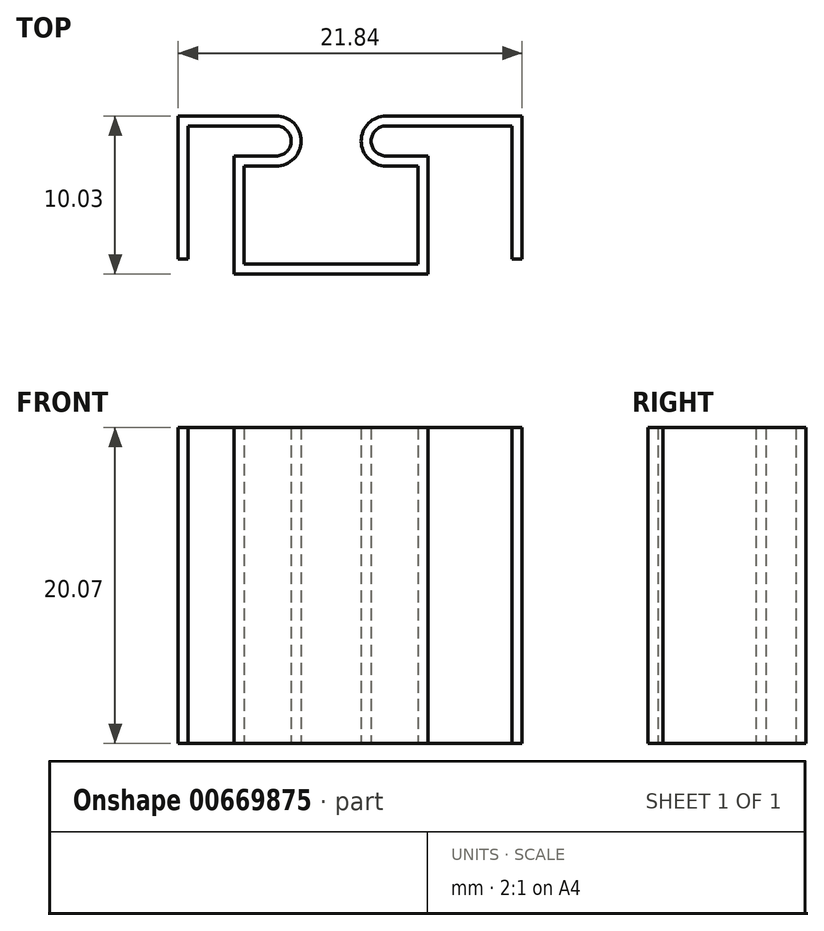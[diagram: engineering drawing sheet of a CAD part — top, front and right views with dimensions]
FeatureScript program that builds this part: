
annotation { "Feature Type Name" : "Feature", "Feature Type Description" : "" }
export const myFeature = defineFeature(function(context is Context, id is Id, definition is map)
    precondition{}
    {
        {
            var Q0;
            Q0=qCreatedBy(makeId("Top.planeOp"),FACE);
            var sketch = newSketch(context, id + "F0", { "sketchPlane" : qUnion([Q0])});
            skLineSegment(sketch, "E0", {"start": v(0, 0) * mm, "end": v(0, 9.1) * mm});
            skLineSegment(sketch, "E1", {"start": v(0, 9.1) * mm, "end": v(6.22, 9.1) * mm});
            skLineSegment(sketch, "E2", {"start": v(4.2, 5.92) * mm, "end": v(4.2, -0.3) * mm});
            skLineSegment(sketch, "E3", {"start": v(4.2, -0.3) * mm, "end": v(15.24, -0.3) * mm});
            skArc(sketch, "E4", {"start": v(6.22, 5.92) * mm, "mid": v(7.81, 7.5) * mm, "end": v(6.22, 9.1) * mm});
            skLineSegment(sketch, "E5", {"start": v(6.22, 5.92) * mm, "end": v(4.2, 5.92) * mm});
            skLineSegment(sketch, "E6.MirrorCS", {"start": v(15.24, 5.92) * mm, "end": v(15.24, -0.3) * mm});
            skLineSegment(sketch, "E7.MirrorCS", {"start": v(13.2, 5.92) * mm, "end": v(15.24, 5.92) * mm});
            skArc(sketch, "E8.MirrorCS", {"start": v(13.2, 5.92) * mm, "mid": v(11.62, 7.5) * mm, "end": v(13.2, 9.1) * mm});
            skLineSegment(sketch, "E9.MirrorCS", {"start": v(21.84, 9.1) * mm, "end": v(13.2, 9.1) * mm});
            skLineSegment(sketch, "E10.MirrorCS", {"start": v(21.84, 0) * mm, "end": v(21.84, 9.1) * mm});
            skLineSegment(sketch, "E11.0", {"start": v(21.2, 0) * mm, "end": v(21.2, 8.46) * mm});
            skArc(sketch, "E11.3", {"start": v(13.2, 6.55) * mm, "mid": v(12.26, 7.5) * mm, "end": v(13.2, 8.46) * mm});
            skArc(sketch, "E11.4", {"start": v(6.22, 6.55) * mm, "mid": v(7.18, 7.5) * mm, "end": v(6.22, 8.46) * mm});
            skLineSegment(sketch, "E11.6", {"start": v(0.63, 8.46) * mm, "end": v(6.22, 8.46) * mm});
            skLineSegment(sketch, "E11.7", {"start": v(0.63, 0) * mm, "end": v(0.63, 8.46) * mm});
            skLineSegment(sketch, "E11.8", {"start": v(6.22, 6.55) * mm, "end": v(3.56, 6.55) * mm});
            skLineSegment(sketch, "E11.9", {"start": v(3.56, 6.55) * mm, "end": v(3.56, -0.94) * mm});
            skLineSegment(sketch, "E11.10", {"start": v(3.56, -0.94) * mm, "end": v(15.88, -0.94) * mm});
            skLineSegment(sketch, "E11.12", {"start": v(15.88, 6.55) * mm, "end": v(15.88, -0.94) * mm});
            skLineSegment(sketch, "E11.13", {"start": v(13.2, 6.55) * mm, "end": v(15.88, 6.55) * mm});
            skLineSegment(sketch, "E12", {"start": v(0.63, 0) * mm, "end": v(0, 0) * mm});
            skLineSegment(sketch, "E13", {"start": v(21.84, 0) * mm, "end": v(21.2, 0) * mm});
            skLineSegment(sketch, "E14", {"start": v(13.2, 8.46) * mm, "end": v(21.2, 8.46) * mm});
            skSolve(sketch);
        }
        {
            var Q0;
            Q0=qSketchRegion(id+"F0",true);
            extrude(context, id + "F1", {"entities" : qUnion([Q0]), "depth" : 20.07 * mm});
        }
    });
